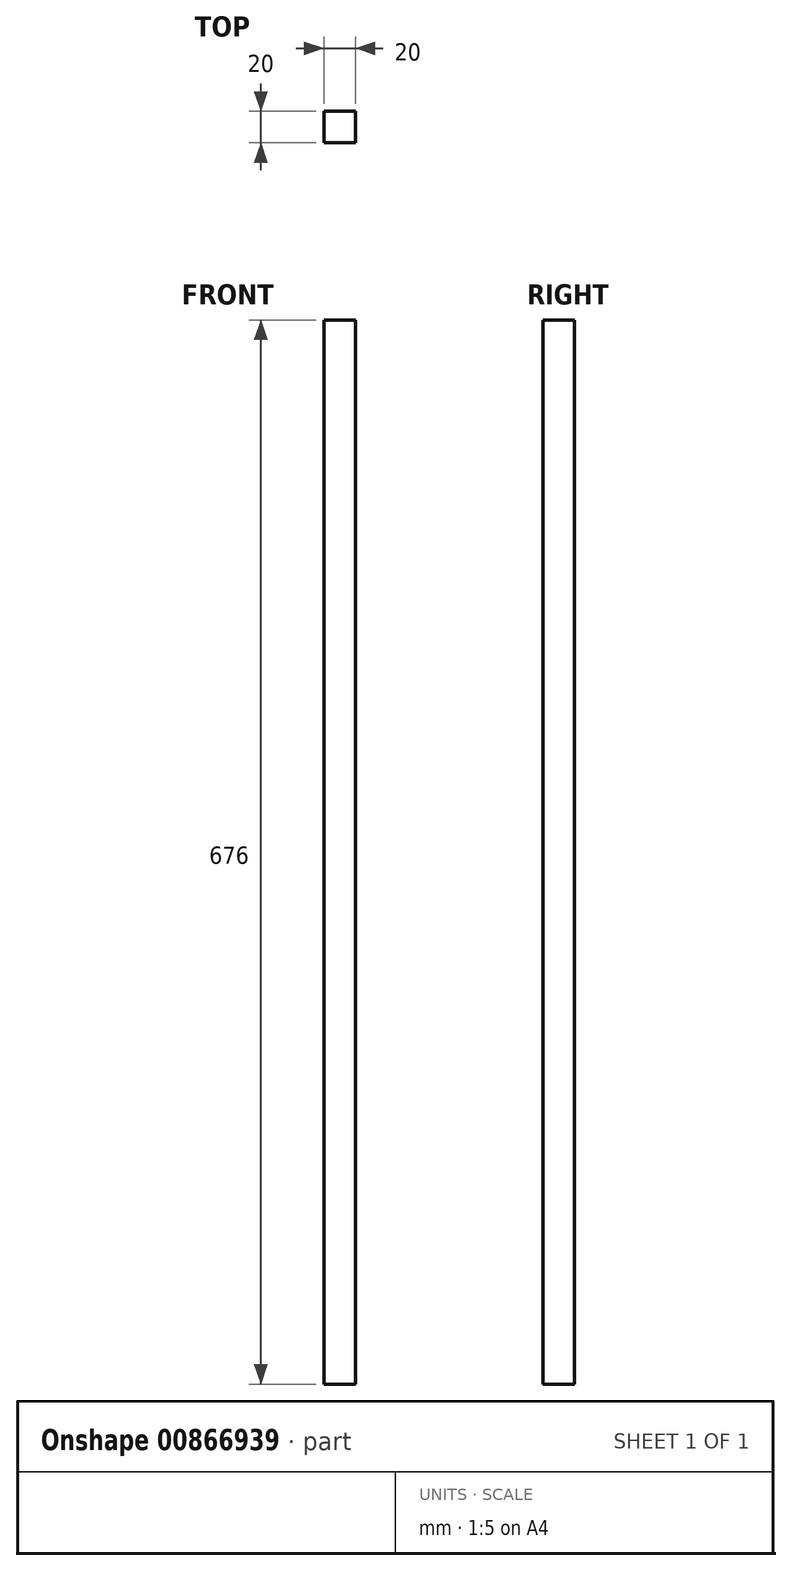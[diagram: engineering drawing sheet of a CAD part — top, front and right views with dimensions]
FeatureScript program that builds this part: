
annotation { "Feature Type Name" : "Feature", "Feature Type Description" : "" }
export const myFeature = defineFeature(function(context is Context, id is Id, definition is map)
    precondition{}
    {
        {
            var Q0;
            Q0=qCreatedBy(makeId("Top.planeOp"),FACE);
            var sketch = newSketch(context, id + "F0", { "sketchPlane" : qUnion([Q0])});
            skLineSegment(sketch, "E0.bottom", {"start": v(-10, 10) * mm, "end": v(10, 10) * mm});
            skLineSegment(sketch, "E0.top", {"start": v(-10, -10) * mm, "end": v(10, -10) * mm});
            skLineSegment(sketch, "E0.left", {"start": v(-10, 10) * mm, "end": v(-10, -10) * mm});
            skLineSegment(sketch, "E0.right", {"start": v(10, 10) * mm, "end": v(10, -10) * mm});
            skSolve(sketch);
        }
        {
            var Q0;
            Q0 = qSketchRegion(id + "F0", true);
            extrude(context, id + "F1", {"entities" : qUnion([Q0]), "depth" : 676 * mm, "offsetDistance" : 25 * mm});
        }
    });
